# Revit family: Shower-Modular_Column-KOHLER-Spaviva-K-EX31847T.rfa_
name_source: partatom
category: Plumbing Fixtures
units: mm (PartAtom-declared; Revit-internal decimal feet)

## family parameters
Cut with Voids When Loaded = No
Host = Face
Maintain Annotation Orientation = No
OmniClass Number = 23.31.17.00
OmniClass Title = Showers
Part Type = Normal
Room Calculation Point = No
Round Connector Dimension = Use Diameter
Shared = No

## types (3) — shared parameters
ADA Compliant = No
Assembly Code = D2010700
CW Connection = Yes
Cold Water Inlet = Cold Water Inlet
Date Modified = 07/09/2025
Default Elevation = 42"
Description = Modular Column - Beauty Version
Drain Included = No
Flow Rate = 3 GPM
HW Connection = Yes
Height = 76 7/8"
Hot Water Inlet = Hot Water Inlet
Length = 18 9/16"
Manufacturer = Kohler Co.
Master Format 2014 = 22 42 23
Master Format 2014 Name = Residential Showers
Material = Premium Metal Construction
Pressure = 0.00 psi
Product Name = Spaviva
URL = http://www.kohler.com.cn
Vent Connection = No
Waste Connection = No
Waste Water Outlet = Waste Water Outlet
WaterSense Certified = No
Width = 23 13/16"

## per-type parameters (varying)
| type | Button Finish | Decorative Ring Finish | Finish | Model | Secondary Finish | Shell Finish | Tray Finish | Type |
| CP-Polished Chrome | Plastic-Pantone-PQ-11-4800-TCX | Kohler-Plastic-0-White | Kohler-Metal-CP-Polished_Chrome | K-EX31847T-9-CP | Plastic-Pantone-PQ-11-4800-TCX | Kohler-Plastic-WPT-White | Plastic-Pantone-PQ-11-4800-TCX | 3 |
| BRD-Brushed Rose Gold | Plastic-Pantone-PQ-11-4800-TCX | Kohler-Plastic-0-White | KOHLER-Metal-BRD-Brushed_Rose_Gold | K-EX31847T-9-BRD | Plastic-Pantone-PQ-11-4800-TCX | Kohler-Plastic-WPT-White | Plastic-Pantone-PQ-11-4800-TCX | 2 |
| 2MB-Vibrant Brushed Moderne Brass | Plastic-Pantone-PQ-194205-TCX | Plastic-Pantone-PQ-194205-TCX | Kohler-Metal-2MB-Vibrant_Brushed_Moderne_Brass | K-EX31847T-9-2MB | Plastic-Pantone-PQ-194205-TCX | Plastic-GPT | Plastic-Pantone-625C | 1 |

## geometry (parser evidence)
native form markers: Sweep x11
no freeform markers — native parametric forms only
